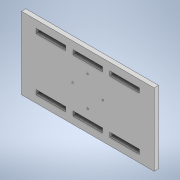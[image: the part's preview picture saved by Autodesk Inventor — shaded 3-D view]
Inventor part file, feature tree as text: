
AUTODESK INVENTOR PART (.ipt)
format: ipt  version: 2022 (Build 260153000, 153)  size: 145,408 bytes
history: native  units: mm
features: extrude x1, sketch x1
ambient origin geometry x8: Origin, YZ Plane, XZ Plane, XY Plane, X Axis, Y Axis, Z Axis, Center Point
bodies: Solid1 (feature_tree)
feature tree (2):
  extrude  "Extrusion1"  Depth=3.0mm TaperAngle=0.0deg
  sketch  "Sketch1"  dims[d3=49.0mm d4=3.0mm d5=0.0mm d6=5.0mm d7=10.0mm d8=20.0mm d11=20.0mm d14=5.0mm d17=24.5mm d19=20.0mm d20=5.0mm d23=20.5mm d24=1.0mm d25=1.0mm d26=1.0mm d27=1.0mm]
